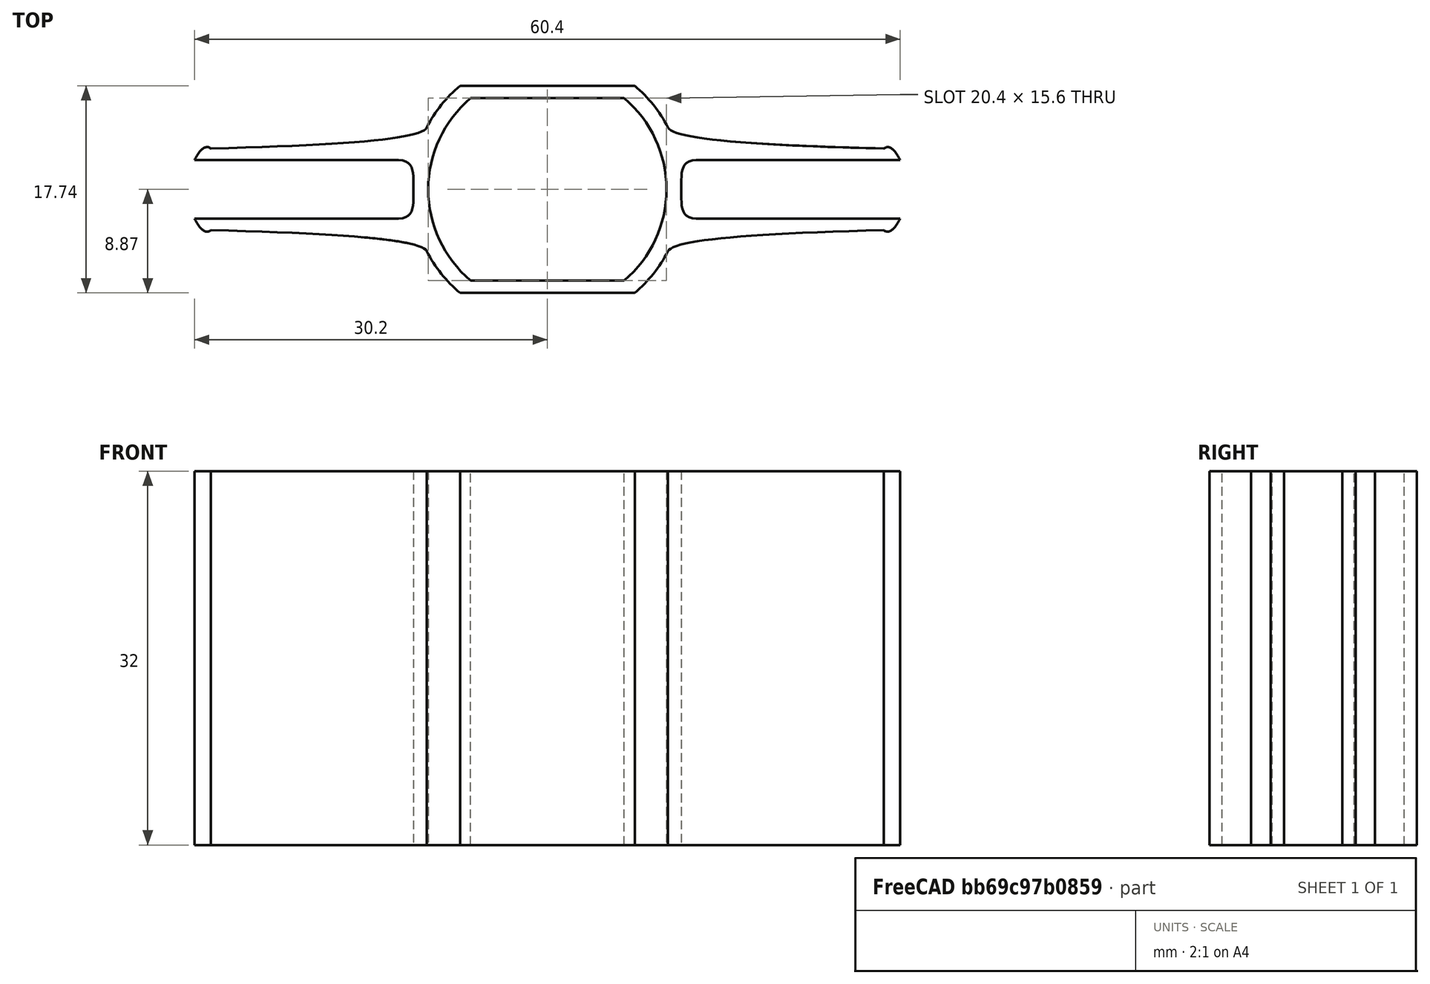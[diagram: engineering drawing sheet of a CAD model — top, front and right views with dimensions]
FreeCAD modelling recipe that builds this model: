
FCSTD DOCUMENT  (FreeCAD 0.19R0.19.2)
Label: 018
License: All rights reserved
LicenseURL: http://en.wikipedia.org/wiki/All_rights_reserved
objects: Sketcher::SketchObject×2, Part::Extrusion×1
note: 3 computed .brp shape members not serialized (recipe doc carries the construction recipe); baked Part::Feature solids carry a one-line shape summary decoded from their .brp

FEATURE [Sketcher::SketchObject] Sketch  label="main001"
  FullyConstrained = true
  sketch-geometry (80):
    g0: ArcOfCircle CenterX=-3.45031e-07 CenterY=0 CenterZ=0 NormalX=0 NormalY=0 NormalZ=1 AngleXU=0 Radius=10.2 StartAngle=5.4126 EndAngle=7.15377
    g1: ArcOfCircle CenterX=-3.45031e-07 CenterY=0 CenterZ=0 NormalX=0 NormalY=0 NormalZ=1 AngleXU=0 Radius=10.2 StartAngle=2.27101 EndAngle=4.01218
    g2: LineSegment StartX=-6.57267 StartY=7.8 StartZ=0 EndX=6.57267 EndY=7.8 EndZ=0
    g3: LineSegment StartX=-6.57267 StartY=-7.8 StartZ=0 EndX=6.57267 EndY=-7.8 EndZ=0
    g4: ArcOfCircle CenterX=-3.45031e-07 CenterY=0 CenterZ=0 NormalX=0 NormalY=0 NormalZ=1 AngleXU=0 Radius=11.6 StartAngle=2.27101 EndAngle=2.66709
    g5: ArcOfCircle CenterX=-3.45031e-07 CenterY=0 CenterZ=0 NormalX=0 NormalY=0 NormalZ=1 AngleXU=0 Radius=11.6 StartAngle=5.4126 EndAngle=5.80868
    g6: LineSegment StartX=-7.4748 StartY=8.87059 StartZ=0 EndX=7.4748 EndY=8.87059 EndZ=0
    g7: LineSegment StartX=-7.4748 StartY=-8.87059 StartZ=0 EndX=7.4748 EndY=-8.87059 EndZ=0
    g8: ArcOfCircle CenterX=-3.45031e-07 CenterY=0 CenterZ=0 NormalX=0 NormalY=0 NormalZ=1 AngleXU=0 Radius=11.6 StartAngle=3.6161 EndAngle=4.01218
    g9: ArcOfCircle CenterX=-3.45031e-07 CenterY=0 CenterZ=0 NormalX=0 NormalY=0 NormalZ=1 AngleXU=0 Radius=11.6 StartAngle=0.474503 EndAngle=0.870585
    g10: Circle CenterX=-28.8 CenterY=3.5 CenterZ=0 NormalX=0 NormalY=0 NormalZ=1 AngleXU=0 Radius=1
    g11: Circle CenterX=-10.9247 CenterY=3.9 CenterZ=0 NormalX=0 NormalY=0 NormalZ=1 AngleXU=0 Radius=1
    g12: Circle CenterX=-10.3184 CenterY=5.3 CenterZ=0 NormalX=0 NormalY=0 NormalZ=1 AngleXU=0 Radius=1
    g13: BSplineCurve PolesCount=3 KnotsCount=2 Degree=2 IsPeriodic=0
    g14: GeomPoint X=-28.8 Y=3.5 Z=0
    g15: GeomPoint X=-10.3184 Y=5.3 Z=0
    g16: Circle CenterX=28.8 CenterY=3.5 CenterZ=0 NormalX=0 NormalY=0 NormalZ=1 AngleXU=0 Radius=1
    g17: Circle CenterX=10.9247 CenterY=3.9 CenterZ=0 NormalX=0 NormalY=0 NormalZ=1 AngleXU=0 Radius=1
    g18: Circle CenterX=10.3184 CenterY=5.3 CenterZ=0 NormalX=0 NormalY=0 NormalZ=1 AngleXU=0 Radius=1
    g19: BSplineCurve PolesCount=3 KnotsCount=2 Degree=2 IsPeriodic=0
    g20: GeomPoint X=28.8 Y=3.5 Z=0
    g21: GeomPoint X=10.3184 Y=5.3 Z=0
    g22: Circle CenterX=-28.8 CenterY=-3.5 CenterZ=0 NormalX=0 NormalY=0 NormalZ=1 AngleXU=0 Radius=1
    g23: Circle CenterX=-10.9247 CenterY=-3.9 CenterZ=0 NormalX=0 NormalY=0 NormalZ=1 AngleXU=0 Radius=1
    g24: Circle CenterX=-10.3184 CenterY=-5.3 CenterZ=0 NormalX=0 NormalY=0 NormalZ=1 AngleXU=0 Radius=1
    g25: BSplineCurve PolesCount=3 KnotsCount=2 Degree=2 IsPeriodic=0
    g26: GeomPoint X=-28.8 Y=-3.5 Z=0
    g27: GeomPoint X=-10.3184 Y=-5.3 Z=0
    g28: Circle CenterX=28.8 CenterY=-3.5 CenterZ=0 NormalX=0 NormalY=0 NormalZ=1 AngleXU=0 Radius=1
    g29: Circle CenterX=10.9247 CenterY=-3.9 CenterZ=0 NormalX=0 NormalY=0 NormalZ=1 AngleXU=0 Radius=1
    g30: Circle CenterX=10.3184 CenterY=-5.3 CenterZ=0 NormalX=0 NormalY=0 NormalZ=1 AngleXU=0 Radius=1
    g31: BSplineCurve PolesCount=3 KnotsCount=2 Degree=2 IsPeriodic=0
    g32: GeomPoint X=28.8 Y=-3.5 Z=0
    g33: GeomPoint X=10.3184 Y=-5.3 Z=0
    g34-g38: Circle x5 (B-spline internal-alignment scaffolding for g39; pole/knot coordinates omitted)
    g39: BSplineCurve PolesCount=5 KnotsCount=3 Degree=3 IsPeriodic=0
    g40: GeomPoint X=12.7274 Y=2.5 Z=0
    g41: GeomPoint X=11.4637 Y=2.49999e-07 Z=0
    g42: GeomPoint X=12.7274 Y=-2.5 Z=0
    g43-g47: Circle x5 (B-spline internal-alignment scaffolding for g48; pole/knot coordinates omitted)
    g48: BSplineCurve PolesCount=5 KnotsCount=3 Degree=3 IsPeriodic=0
    g49: GeomPoint X=-12.7274 Y=2.5 Z=0
    g50: GeomPoint X=-11.4637 Y=2.50004e-07 Z=0
    g51: GeomPoint X=-12.7274 Y=-2.5 Z=0
    g52: LineSegment StartX=-30.2 StartY=-2.5 StartZ=0 EndX=-12.7274 EndY=-2.5 EndZ=0
    g53: LineSegment StartX=-30.2 StartY=2.5 StartZ=0 EndX=-12.7274 EndY=2.5 EndZ=0
    g54: LineSegment StartX=30.2 StartY=2.5 StartZ=0 EndX=12.7274 EndY=2.5 EndZ=0
    g55: LineSegment StartX=30.2 StartY=-2.5 StartZ=0 EndX=12.7274 EndY=-2.5 EndZ=0
    g56: Circle CenterX=-30.2 CenterY=2.5 CenterZ=0 NormalX=0 NormalY=0 NormalZ=1 AngleXU=0 Radius=1
    g57: Circle CenterX=-29.4304 CenterY=3.99253 CenterZ=0 NormalX=0 NormalY=0 NormalZ=1 AngleXU=0 Radius=1
    g58: Circle CenterX=-28.8 CenterY=3.5 CenterZ=0 NormalX=0 NormalY=0 NormalZ=1 AngleXU=0 Radius=1
    g59: BSplineCurve PolesCount=3 KnotsCount=2 Degree=2 IsPeriodic=0
    g60: GeomPoint X=-30.2 Y=2.5 Z=0
    g61: GeomPoint X=-28.8 Y=3.5 Z=0
    g62: Circle CenterX=30.2 CenterY=-2.5 CenterZ=0 NormalX=0 NormalY=0 NormalZ=1 AngleXU=0 Radius=1
    g63: Circle CenterX=29.4304 CenterY=-3.99253 CenterZ=0 NormalX=0 NormalY=0 NormalZ=1 AngleXU=0 Radius=1
    g64: Circle CenterX=28.8 CenterY=-3.5 CenterZ=0 NormalX=0 NormalY=0 NormalZ=1 AngleXU=0 Radius=1
    g65: BSplineCurve PolesCount=3 KnotsCount=2 Degree=2 IsPeriodic=0
    g66: GeomPoint X=30.2 Y=-2.5 Z=0
    g67: GeomPoint X=28.8 Y=-3.5 Z=0
    g68: Circle CenterX=30.2 CenterY=2.5 CenterZ=0 NormalX=0 NormalY=0 NormalZ=1 AngleXU=0 Radius=1
    g69: Circle CenterX=29.4304 CenterY=3.99253 CenterZ=0 NormalX=0 NormalY=0 NormalZ=1 AngleXU=0 Radius=1
    g70: Circle CenterX=28.8 CenterY=3.5 CenterZ=0 NormalX=0 NormalY=0 NormalZ=1 AngleXU=0 Radius=1
    g71: BSplineCurve PolesCount=3 KnotsCount=2 Degree=2 IsPeriodic=0
    g72: GeomPoint X=30.2 Y=2.5 Z=0
    g73: GeomPoint X=28.8 Y=3.5 Z=0
    g74: Circle CenterX=-30.2 CenterY=-2.5 CenterZ=0 NormalX=0 NormalY=0 NormalZ=1 AngleXU=0 Radius=1
    g75: Circle CenterX=-29.4304 CenterY=-3.99253 CenterZ=0 NormalX=0 NormalY=0 NormalZ=1 AngleXU=0 Radius=1
    g76: Circle CenterX=-28.8 CenterY=-3.5 CenterZ=0 NormalX=0 NormalY=0 NormalZ=1 AngleXU=0 Radius=1
    g77: BSplineCurve PolesCount=3 KnotsCount=2 Degree=2 IsPeriodic=0
    g78: GeomPoint X=-30.2 Y=-2.5 Z=0
    g79: GeomPoint X=-28.8 Y=-3.5 Z=0
  constraints (131):
    c: Block(g0)
    c: Equal(g0,g1)
    c: Coincident(g0,g1)
    c: Coincident(g2,g1)
    c: Coincident(g2,g0)
    c: Horizontal(g2)
    c: Coincident(g3,g1)
    c: Coincident(g3,g0)
    c: Horizontal(g3)
    c: Block(g2)
    c: Block(g3)
    c: Coincident(g4,g0)
    c: Coincident(g5,g0)
    c: Block(g5)
    c: Block(g4)
    c: Coincident(g6,g4)
    c: Coincident(g6,g9)
    c: Horizontal(g6)
    c: Coincident(g7,g8)
    c: Coincident(g7,g5)
    c: Horizontal(g7)
    c: Equal(g4,g8)
    c: Coincident(g4,g8)
    c: Equal(g5,g9)
    c: Coincident(g5,g9)
    c: Block(g8)
    c: Block(g9)
    c: Weight(g10) = 1
    c: Equal(g10,g11)
    c: Equal(g10,g12)
    c: Coincident(g13,g4)
    c: InternalAlignment(g10,g13)
    c: InternalAlignment(g11,g13)
    c: InternalAlignment(g12,g13)
    c: InternalAlignment(g14,g13)
    c: InternalAlignment(g15,g13)
    c: Weight(g16) = 1
    c: Equal(g16,g17)
    c: Equal(g16,g18)
    c: Coincident(g19,g9)
    c: InternalAlignment(g16,g19)
    c: InternalAlignment(g17,g19)
    c: InternalAlignment(g18,g19)
    c: InternalAlignment(g20,g19)
    c: InternalAlignment(g21,g19)
    c: Weight(g22) = 1
    c: Equal(g22,g23)
    c: Equal(g22,g24)
    c: Coincident(g25,g8)
    c: InternalAlignment(g22,g25)
    c: InternalAlignment(g23,g25)
    c: InternalAlignment(g24,g25)
    c: InternalAlignment(g26,g25)
    c: InternalAlignment(g27,g25)
    c: Weight(g28) = 1
    c: Equal(g28,g29)
    c: Equal(g28,g30)
    c: Coincident(g31,g5)
    c: InternalAlignment(g28,g31)
    c: InternalAlignment(g29,g31)
    c: InternalAlignment(g30,g31)
    c: InternalAlignment(g32,g31)
    c: InternalAlignment(g33,g31)
    c: Block(g19)
    c: Block(g13)
    c: Block(g31)
    c: Block(g25)
    c: Weight(g34) = 1
    c: Equal(g34, g35-g38) x4
    c: InternalAlignment(g34-g38 -> g39) x5
    c: InternalAlignment(g40,g39)
    c: InternalAlignment(g41,g39)
    c: InternalAlignment(g42,g39)
    c: Weight(g43) = 1
    c: Equal(g43,g44)
    c: Equal(g43,g45)
    c: Equal(g43,g46)
    c: InternalAlignment(g43-g47 -> g48) x5
    c: InternalAlignment(g49,g48)
    c: InternalAlignment(g50,g48)
    c: InternalAlignment(g51,g48)
    c: Block(g48)
    c: Block(g39)
    c: Coincident(g52,g48)
    c: Tangent(g52,g22)
    c: Coincident(g53,g48)
    c: Tangent(g53,g10)
    c: Coincident(g54,g39)
    c: Tangent(g54,g16)
    c: Coincident(g55,g39)
    c: Tangent(g55,g28)
    c: Weight(g56) = 1
    c: Equal(g56,g57)
    c: Equal(g56,g58)
    c: InternalAlignment(g56,g59)
    c: InternalAlignment(g57,g59)
    c: InternalAlignment(g58,g59)
    c: InternalAlignment(g60,g59)
    c: InternalAlignment(g61,g59)
    c: Weight(g62) = 1
    c: Equal(g62,g63)
    c: Equal(g62,g64)
    c: InternalAlignment(g62,g65)
    c: InternalAlignment(g63,g65)
    c: InternalAlignment(g64,g65)
    c: InternalAlignment(g66,g65)
    c: InternalAlignment(g67,g65)
    c: Weight(g68) = 1
    c: Equal(g68,g69)
    c: Equal(g68,g70)
    c: InternalAlignment(g68,g71)
    c: InternalAlignment(g69,g71)
    c: InternalAlignment(g70,g71)
    c: InternalAlignment(g72,g71)
    c: InternalAlignment(g73,g71)
    c: Block(g71)
    c: Block(g54)
    c: Block(g65)
    c: Block(g55)
    c: Weight(g74) = 1
    c: Equal(g74,g75)
    c: Equal(g74,g76)
    c: InternalAlignment(g74,g77)
    c: InternalAlignment(g75,g77)
    c: InternalAlignment(g76,g77)
    c: InternalAlignment(g78,g77)
    c: InternalAlignment(g79,g77)
    c: Block(g77)
    c: Block(g52)
    c: Block(g59)
    c: Block(g53)
FEATURE [Part::Extrusion] Extrude  label="main"
  Base = -> Sketch
  Dir = (0,0,1)
  DirMode = 2
  FaceMakerClass = Part::FaceMakerBullseye
  LengthFwd = 32
  LengthRev = 0
  Solid = true
  Symmetric = false
FEATURE [Sketcher::SketchObject] Sketch001  label="mainCollingAndStructuralHoles"
  FullyConstrained = true
  Placement = pos=(0,0,0) rot=(-1,0,0;4.71239rad)
  sketch-geometry (26):
    g0: Circle CenterX=-5 CenterY=2 CenterZ=0 NormalX=0 NormalY=0 NormalZ=1 AngleXU=0 Radius=1
    g1: Circle CenterX=-5 CenterY=0 CenterZ=0 NormalX=0 NormalY=0 NormalZ=1 AngleXU=0 Radius=1
    g2: Circle CenterX=-3 CenterY=4.6505e-12 CenterZ=0 NormalX=0 NormalY=0 NormalZ=1 AngleXU=0 Radius=1
    g3: BSplineCurve PolesCount=3 KnotsCount=2 Degree=2 IsPeriodic=0
    g4: GeomPoint X=-5 Y=2 Z=0
    g5: GeomPoint X=-3 Y=4.6505e-12 Z=0
    g6: Circle CenterX=5 CenterY=2 CenterZ=0 NormalX=0 NormalY=0 NormalZ=1 AngleXU=0 Radius=1
    g7: Circle CenterX=5 CenterY=4.6505e-12 CenterZ=0 NormalX=0 NormalY=0 NormalZ=1 AngleXU=0 Radius=1
    g8: Circle CenterX=3 CenterY=4.6505e-12 CenterZ=0 NormalX=0 NormalY=0 NormalZ=1 AngleXU=0 Radius=1
    g9: BSplineCurve PolesCount=3 KnotsCount=2 Degree=2 IsPeriodic=0
    g10: GeomPoint X=5 Y=2 Z=0
    g11: GeomPoint X=3 Y=4.6505e-12 Z=0
    g12: LineSegment StartX=5 StartY=2 StartZ=0 EndX=5 EndY=10 EndZ=0
    g13: LineSegment StartX=-5 StartY=2 StartZ=0 EndX=-5 EndY=10 EndZ=0
    g14: LineSegment StartX=-3 StartY=4.6505e-12 StartZ=0 EndX=3 EndY=4.6505e-12 EndZ=0
    g15: LineSegment StartX=-5 StartY=10 StartZ=0 EndX=5 EndY=10 EndZ=0
    g16: LineSegment StartX=-5 StartY=-7 StartZ=0 EndX=5 EndY=-7 EndZ=0
    g17: LineSegment StartX=-5 StartY=-7 StartZ=0 EndX=-5 EndY=-16 EndZ=0
    g18: LineSegment StartX=-5 StartY=-16 StartZ=0 EndX=5 EndY=-16 EndZ=0
    g19: LineSegment StartX=5 StartY=-7 StartZ=0 EndX=5 EndY=-16 EndZ=0
    g20: LineSegment StartX=5 StartY=-7 StartZ=0 EndX=5 EndY=-8.4 EndZ=0
    g21: LineSegment StartX=-5 StartY=-7 StartZ=0 EndX=-5 EndY=-8.4 EndZ=0
    g22: LineSegment StartX=5 StartY=-16 StartZ=0 EndX=5 EndY=-14.6 EndZ=0
    g23: LineSegment StartX=-5 StartY=-16 StartZ=0 EndX=-5 EndY=-14.6 EndZ=0
    g24: LineSegment StartX=5 StartY=-16 StartZ=0 EndX=3.6 EndY=-16 EndZ=0
    g25: LineSegment StartX=5 StartY=-7 StartZ=0 EndX=3.6 EndY=-7 EndZ=0
  constraints (60):
    c: Weight(g0) = 1
    c: Equal(g0,g1)
    c: Equal(g0,g2)
    c: InternalAlignment(g0,g3)
    c: InternalAlignment(g1,g3)
    c: InternalAlignment(g2,g3)
    c: InternalAlignment(g4,g3)
    c: InternalAlignment(g5,g3)
    c: Weight(g6) = 1
    c: Equal(g6,g7)
    c: Equal(g6,g8)
    c: InternalAlignment(g6,g9)
    c: InternalAlignment(g7,g9)
    c: InternalAlignment(g8,g9)
    c: InternalAlignment(g10,g9)
    c: InternalAlignment(g11,g9)
    c: Block(g3)
    c: Coincident(g13,g3)
    c: Block(g9)
    c: Coincident(g12,g9)
    c: Vertical(g12)
    c: Block(g12)
    c: Block(g13)
    c: Coincident(g14,g3)
    c: Coincident(g14,g9)
    c: Horizontal(g14)
    c: Coincident(g15,g13)
    c: Coincident(g15,g12)
    c: Horizontal(g15)
    c: Distance(g12) = 8
    c: Distance(g15) = 10
    c: Horizontal(g16)
    c: Equal(g15,g16) = 10
    c: Vertical(g17)
    c: Distance(g17) = 9
    c: Horizontal(g18)
    c: Coincident(g18,g17)
    c: Block(g18)
    c: Block(g16)
    c: Coincident(g19,g16)
    c: Coincident(g19,g18)
    c: Vertical(g19)
    c: Vertical(g20)
    c: Distance(g20) = 1.4
    c: Vertical(g21)
    c: Equal(g20,g21) = 1.4
    c: Coincident(g21,g16)
    c: Coincident(g20,g16)
    c: Vertical(g22)
    c: Distance(g22) = 1.4
    c: Vertical(g23)
    c: Equal(g22,g23) = 1.4
    c: Coincident(g23,g17)
    c: Coincident(g22,g18)
    c: Horizontal(g24)
    c: Distance(g24) = 1.4
    c: Horizontal(g25)
    c: Equal(g24,g25) = 1.4
    c: Coincident(g25,g16)
    c: Coincident(g24,g18)
